# Revit family: Kohler Instaflush 77028IN-M-NA Family
name_source: partatom
category: Generic Models
revit_build: Autodesk Revit 2018 (Build: 20180329_1100(x64)
units: mm (PartAtom-declared; Revit-internal decimal feet)

## family parameters
Always vertical = Yes
Can host rebar = No
Cut with Voids When Loaded = No
Part Type = Normal
Room Calculation Point = No
Round Connector Dimension = Use Diameter
Shared = No
Work Plane-Based = No

## types (1)
- Kohler 77028IN-M-NA
    Description = In-Wall tank with full Frame
    Fill Up Tank = 3.0 Pa
    Guarantees = No Leakages, 50 Years of use
    Height = 1127 mm  [stored 3.69751 ft]
    Length = 560 mm  [stored 1.83727 ft]
    Manufacturer = Kohler
    Material Frame = frame
    Material Name = holes
    Material Stand = Gold
    Material Water Can = White
    Model = Kohler InstaFlush 77028IN-M-NA
    Type Image = 77028IN-M-NA.tif
    URL = http://www.us.kohler.com
    Width = 40 mm  [stored 0.131234 ft]

note: [stored X ft] marks values corroborated as IEEE doubles in the binary element streams (Revit-internal decimal feet)

## geometry (parser evidence)
native form markers: Sweep x2
no freeform markers — native parametric forms only
